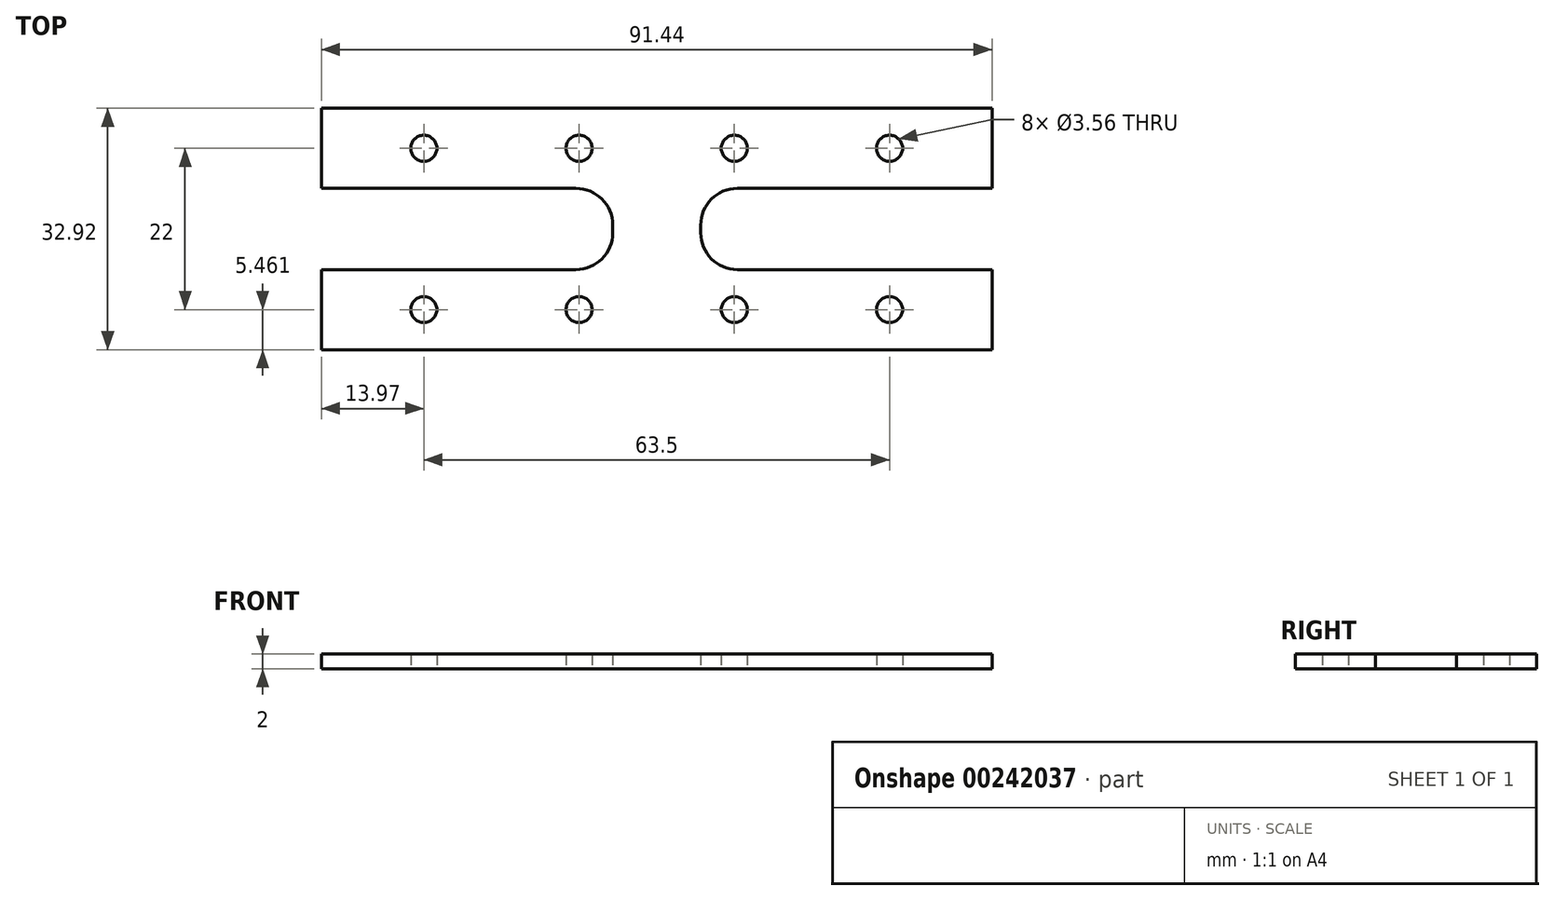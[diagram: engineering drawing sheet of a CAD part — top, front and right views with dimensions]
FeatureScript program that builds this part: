
annotation { "Feature Type Name" : "Feature", "Feature Type Description" : "" }
export const myFeature = defineFeature(function(context is Context, id is Id, definition is map)
    precondition{}
    {
        {
            var Q0;
            Q0=qCreatedBy(makeId("Top.planeOp"),FACE);
            var sketch = newSketch(context, id + "F0", { "sketchPlane" : qUnion([Q0])});
            skLineSegment(sketch, "E0.bottom", {"start": v(0, 0) * mm, "end": v(91.44, 0) * mm});
            skLineSegment(sketch, "E0.top", {"start": v(0, 10.92) * mm, "end": v(34.72, 10.92) * mm});
            skLineSegment(sketch, "E0.left", {"start": v(0, 0) * mm, "end": v(0, 10.92) * mm});
            skLineSegment(sketch, "E0.right", {"start": v(91.44, 0) * mm, "end": v(91.44, 10.92) * mm});
            skLineSegment(sketch, "E1", {"start": v(45.72, 10.92) * mm, "end": v(45.72, 0) * mm, "construction": true});
            skCircle(sketch, "E2", {"center": v(13.97, 5.46) * mm, "radius": 1.78 * mm});
            skLineSegment(sketch, "E3", {"start": v(0, 5.46) * mm, "end": v(45.72, 5.46) * mm, "construction": true});
            skCircle(sketch, "E4.1.0.0", {"center": v(35.14, 5.46) * mm, "radius": 1.78 * mm});
            skCircle(sketch, "E4.2.0.0", {"center": v(56.3, 5.46) * mm, "radius": 1.78 * mm});
            skCircle(sketch, "E4.3.0.0", {"center": v(77.47, 5.46) * mm, "radius": 1.78 * mm});
            skLineSegment(sketch, "E4.direction1", {"start": v(13.97, 5.46) * mm, "end": v(35.14, 5.46) * mm, "construction": true});
            skLineSegment(sketch, "E5.0.1.0", {"start": v(0, 27.46) * mm, "end": v(45.72, 27.46) * mm, "construction": true});
            skLineSegment(sketch, "E5.0.1.1", {"start": v(13.97, 27.46) * mm, "end": v(35.14, 27.46) * mm, "construction": true});
            skLineSegment(sketch, "E5.0.1.2", {"start": v(0, 22) * mm, "end": v(34.72, 22) * mm});
            skLineSegment(sketch, "E5.0.1.3", {"start": v(0, 32.92) * mm, "end": v(91.44, 32.92) * mm});
            skLineSegment(sketch, "E5.0.1.4", {"start": v(0, 22) * mm, "end": v(0, 32.92) * mm});
            skLineSegment(sketch, "E5.0.1.5", {"start": v(91.44, 22) * mm, "end": v(91.44, 32.92) * mm});
            skLineSegment(sketch, "E5.0.1.6", {"start": v(45.72, 32.92) * mm, "end": v(45.72, 22) * mm, "construction": true});
            skCircle(sketch, "E5.0.1.7", {"center": v(35.14, 27.46) * mm, "radius": 1.78 * mm});
            skCircle(sketch, "E5.0.1.8", {"center": v(13.97, 27.46) * mm, "radius": 1.78 * mm});
            skCircle(sketch, "E5.0.1.9", {"center": v(56.3, 27.46) * mm, "radius": 1.78 * mm});
            skCircle(sketch, "E5.0.1.10", {"center": v(77.47, 27.46) * mm, "radius": 1.78 * mm});
            skLineSegment(sketch, "E5.direction1", {"start": v(0, 0) * mm, "end": v(25, 0) * mm, "construction": true});
            skLineSegment(sketch, "E5.direction2", {"start": v(0, 0) * mm, "end": v(0, 22) * mm, "construction": true});
            skLineSegment(sketch, "E6", {"start": v(39.72, 15.92) * mm, "end": v(39.72, 17) * mm});
            skLineSegment(sketch, "E7.MirrorCS", {"start": v(51.72, 15.92) * mm, "end": v(51.72, 17) * mm});
            skLineSegment(sketch, "E8.trimOffspring", {"start": v(56.72, 22) * mm, "end": v(91.44, 22) * mm});
            skLineSegment(sketch, "E9.trimOffspring", {"start": v(56.72, 10.92) * mm, "end": v(91.44, 10.92) * mm});
            skPoint(sketch, "E10.visualSharp", {"position": v(39.72, 22) * mm});
            skArc(sketch, "E10.filletArc", {"start": v(39.72, 17) * mm, "mid": v(38.26, 20.54) * mm, "end": v(34.72, 22) * mm});
            skPoint(sketch, "E11.visualSharp", {"position": v(51.72, 22) * mm});
            skArc(sketch, "E11.filletArc", {"start": v(56.72, 22) * mm, "mid": v(53.18, 20.54) * mm, "end": v(51.72, 17) * mm});
            skPoint(sketch, "E12.visualSharp", {"position": v(51.72, 10.92) * mm});
            skArc(sketch, "E12.filletArc", {"start": v(51.72, 15.92) * mm, "mid": v(53.18, 12.39) * mm, "end": v(56.72, 10.92) * mm});
            skPoint(sketch, "E13.visualSharp", {"position": v(39.72, 10.92) * mm});
            skArc(sketch, "E13.filletArc", {"start": v(34.72, 10.92) * mm, "mid": v(38.26, 12.39) * mm, "end": v(39.72, 15.92) * mm});
            skSolve(sketch);
        }
        {
            var Q0;
            Q0 = qSketchRegion(id + "F0", true);
            extrude(context, id + "F1", {"entities" : qUnion([Q0]), "depth" : 2 * mm});
        }
    });
